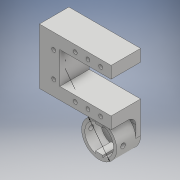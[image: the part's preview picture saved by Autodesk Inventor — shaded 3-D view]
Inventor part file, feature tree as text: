
AUTODESK INVENTOR PART (.ipt)
format: ipt  version: 2018 (Build 220112000, 112)  size: 228,352 bytes
history: native  units: mm
features: sketch x9, extrude x8, other x2, fillet x1, hole x1
ambient origin geometry x8: Origin, YZ Plane, XZ Plane, XY Plane, X Axis, Y Axis, Z Axis, Center Point
bodies: Solide1 (feature_tree)
feature tree (21):
  other  "Annotations"
  extrude  "Extrusion1"  Depth=22.0mm
  extrude  "Extrusion2"  Depth=19.0mm
  extrude  "Extrusion3"  Depth=5.0mm TaperAngle=0.0deg
  extrude  "Extrusion5"  Depth=22.0mm
  extrude  "Extrusion14"  Depth=10.0mm TaperAngle=0.0deg
  extrude  "Extrusion15"  Depth=10.0mm TaperAngle=0.0deg
  extrude  "Extrusion13"  TaperAngle=0.0deg  [1 undecoded]
  fillet  "Congé1"  Radius=9.0mm
  sketch  "Esquisse1"
  sketch  "Esquisse2"
  sketch  "Esquisse3"
  sketch  "Esquisse5"
  sketch  "Esquisse18"
  sketch  "Esquisse19"
  hole  "Perçage3"  [1 undecoded]
  sketch  "Esquisse14"
  sketch  "Esquisse15"
  sketch  "Esquisse17"
  other  "Cote de diamètre 1"
  extrude  "Extrusion11"  Depth=3.0mm
note: 2 required parameter values undecoded (feature->parameter linkage not recoverable at this tier; creation-order binding heuristic only, values carry confidence <= 0.55)
